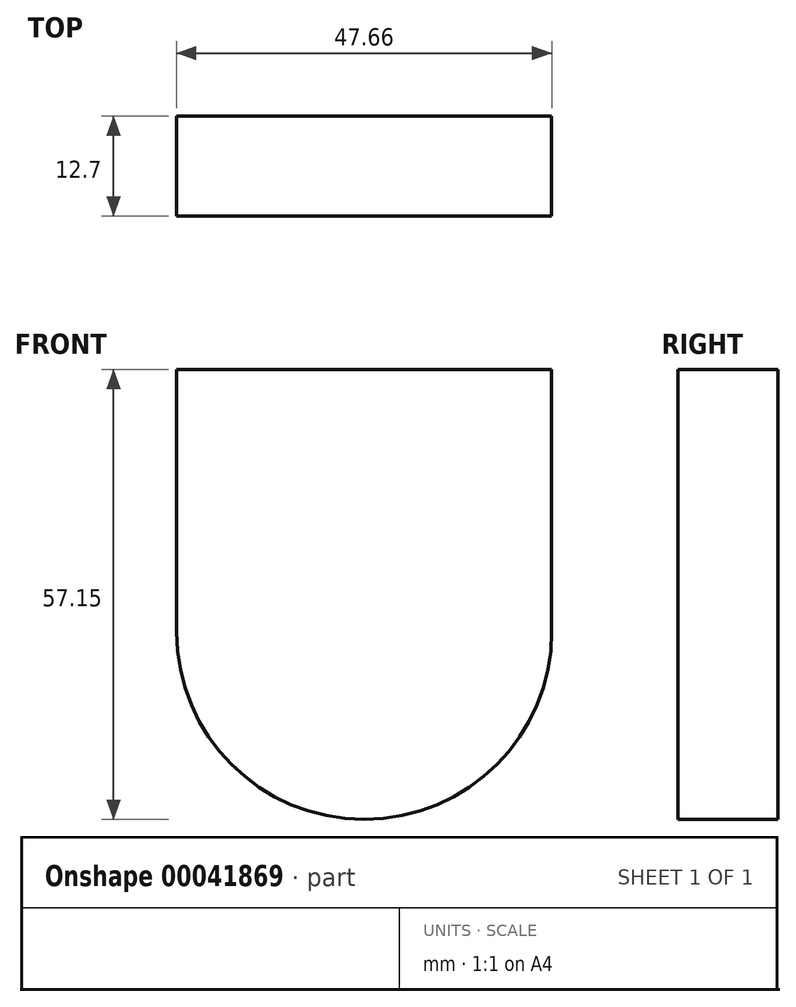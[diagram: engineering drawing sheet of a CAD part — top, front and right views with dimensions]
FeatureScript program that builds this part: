
annotation { "Feature Type Name" : "Feature", "Feature Type Description" : "" }
export const myFeature = defineFeature(function(context is Context, id is Id, definition is map)
    precondition{}
    {
        {
            var Q0;
            Q0=qCreatedBy(makeId("Front.planeOp"),FACE);
            var sketch = newSketch(context, id + "F0", { "sketchPlane" : qUnion([Q0])});
            skLineSegment(sketch, "E0", {"start": v(-23.83, 0) * mm, "end": v(23.83, 0) * mm});
            skLineSegment(sketch, "E1", {"start": v(-23.83, 0) * mm, "end": v(-23.83, -33.32) * mm});
            skLineSegment(sketch, "E2", {"start": v(23.83, 0) * mm, "end": v(23.83, -27.33) * mm});
            skLineSegment(sketch, "E3", {"start": v(0, 0) * mm, "end": v(0, -29.37) * mm});
            skLineSegment(sketch, "E4", {"start": v(0, -57.15) * mm, "end": v(0, -57.15) * mm});
            skLineSegment(sketch, "E5", {"start": v(23.83, -33.32) * mm, "end": v(23.83, -27.33) * mm});
            skPoint(sketch, "E6.visualSharp", {"position": v(-23.83, -57.15) * mm});
            skArc(sketch, "E6.filletArc", {"start": v(-23.83, -33.32) * mm, "mid": v(-16.85, -50.17) * mm, "end": v(0, -57.15) * mm});
            skPoint(sketch, "E7.visualSharp", {"position": v(23.83, -57.15) * mm});
            skArc(sketch, "E7.filletArc", {"start": v(0, -57.15) * mm, "mid": v(16.85, -50.17) * mm, "end": v(23.83, -33.32) * mm});
            skSolve(sketch);
        }
        {
            var Q0;
            {var subQ2=sQuery(id+"F0.wireOp",EDGE,"E1");Q0=makeQuery(id+"F0.imprint","IMPRINT",FACE,{"disambiguationData":[TD([[makeQuery(id+"F0.imprint","IMPRINT",EDGE,{"derivedFrom":subQ2}),1.0]])]});}
            extrude(context, id + "F1", {"entities" : qUnion([Q0]), "oppositeDirection" : true, "depth" : 12.7 * mm});
        }
    });
